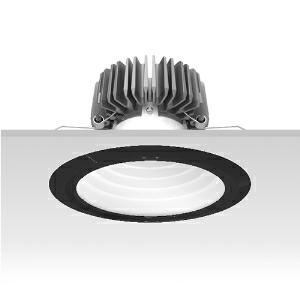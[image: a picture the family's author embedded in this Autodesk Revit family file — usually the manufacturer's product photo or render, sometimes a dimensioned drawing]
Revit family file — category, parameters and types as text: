
# Revit family: 3f_filippi_-_3f_reno_bianco_ampio_3f_filippi_-_30641_a01026_-_3f_reno_200_wh_4000-930_wide___vt_bk_7989
name_source: partatom
category: Lighting Fixtures
units: mm (PartAtom-declared; Revit-internal decimal feet)

## family parameters
Cut with Voids When Loaded = No
Host = Face
Light Source = No
Part Type = Normal
Room Calculation Point = No
Round Connector Dimension = Use Diameter
Shared = No

## types (1)
- 3F Filippi - 3F Reno Bianco Ampio (1 x LED, 3064 lm, 43 W, 3000 K)
    Apparent Load = 43 VA
    Approval mark = CE
    CIE Flux Codes = 75 94 99 100 100
    Color Rendering = 90
    Color Temperature = 3000 K
    Control Gear = Electronic ballast
    Default Elevation = 1800 mm
    Description = ILLUMINOTECHNICAL
Luminous efficiency 100% (DLOR 100%, ULOR 0%).
Initial luminous flux of the luminaire 3064 lm.
Direct symmetric wide distribution.
Installation Interdistance Transv.D = 1.56 x hu - Long.D = 1.56 x hu.
Tabular UGR (CIE 117 - 4H-8H; S=0.25H; 70/50/20): RUG 22.4 - 22.3.
Beam angle: 74° - 74°.
Luminous efficacy 71 lm/W.
Lifetime (L90/B10): 30000 h. (tq+25°C)
Lifetime (L85/B10): 50000 h. (tq+25°C)
Lifetime (L70/B10): 80000 h. (tq+25°C)
Sudden decreased luminous flux after 50000 hours: 0% (C0).
Photobiological safety in compliance with IEC/TR 62778: RG1 low risk, (IEC 62471).
In compliance with IEC/EN 62722-2-1 - IEC/EN 62717 standards.

SOURCE
Compact LED module 4000/930.
Energy efficiency class (UE 2019/2020 - UE 2019/2015): F.
CIE 13.3 Colour rendering index: CRI >90 (R9 >50%).
IES TM-30 Fidelity Index: Rf = 92 Rg = 101.
CCT nominal colour temperature 3000 K.
Colour initial tolerance (MacAdam): SDCM 3.
Zhaga Book 3 compliant.

MECHANICAL
Passive heat dissipator in die-casting aluminium, oversized, for optimum thermal management of the LED module.
Parabolic element with graduated/concentric rings in white polycarbonate.
Transparent external lens with glossy and satin differentiated surfaces, with a cooling and anti-insect system in methacrylate (PMMA).
Fastening spring clips in stainless steel.
Dimensions: diameter 226 mm, height 146 mm. Weight 1.705 kg.
IP44 protection degree for exposed part, IP20 for recessed part.
Mechanical strength to impacts IK06 (1 joule).
Glow-wire test resistance 650°C.

ELECTRICAL
Wiring on a separate unit.
Halogen Free electronic wiring 230V-50/60Hz, power factor 0.95, THD <25%, constant output current, SELV, class II, 1 driver.
Power of the luminaire 43 W.
ENEC - CE.
SAFE FLICKER: PstLM=<1 and SVM=<0.4 (IEC TR 61547-1 and IEC TR 63158), to ensure a more comfortable and safe light.
Luminaire compliant with EN 60598-2-22 for power supply from a centralised emergency system CPSS (Central Power Supply System), not incorporated in the luminaire - high risk areas excluded. The default power and flux are 100% in AC and 100% in DC.
Ambient temperature from 0°C to +25°C.
Temperature class T6 max 85°C.
Relative humidity UR: <85%.

INSTALLATION
Pull-up recessed fitting.
False ceiling carving: 200 mm.
All accessories dedicated to this product are available on the Catalog and on our website www.3F-Filippi.com.

ACCESSORIES
A01026 - VT transparent glass, tempered, not flammable, locked and in line with the trim, in black polycarbonate.

APPLICATIONS
Environments: architectural, commercial, exhibition areas, transit areas, corridors, shops, display windows, service areas.
In false ceilings with narrow voids.

WARNING
Luminaire designed for disposal/recycling at end-of-life.
Replaceable (LED only) light source by a professional. Replaceable control gear by a professional.
    Height = 0 mm  [stored 0 ft]
    Lamp = 1 x LED
    Lamp Light Flux = 3064 lm
    Lamp Power = 43 W
    Lamp count = 1
    Length = 226 mm
    Lifetime = 50000 h
    Luminous efficacy = 71 lm/W
    Manufacturer = 3F Filippi
    ModVariant = No
    Model = 3F Filippi - 30641+A01026 - 3F Reno 200 WH 4000-930 WIDE + VT BK
    Mounting Place = Ceiling
    Mounting Type = Recessed
    Number of Poles = 1
    OnlyDefault = Yes
    Power Factor = 1
    Product Name = 3F Filippi - 3F Reno Bianco Ampio
    Product group = recessed luminaire
    ProductGroupID = 4
    Protection Class = Protection class II
    Protection Degree = IP 20
    RLX_Detail_Level = 1
    RLX_Emergency_Light_Flux = 0 lm
    RLX_Emergency_Type = 0
    RLX_Emergency_Type_DB = No
    RlxData = <blob elided: 100677 chars, md5=1bf3c242>
    Socket = socket
    Standby Power = 0 W
    System Light Flux = 3064 lm
    System Power = 43 W
    Type Comments = Product without accessories
    Type Image = 3ffilippi_3f_reno_200_wh__a01026.jpg
    URL = http://relux.com
    VarID = ---
    Voltage = 0 V
    Weight = 0.00 kg
    Width = 0 mm  [stored 0 ft]

note: [stored X ft] marks values corroborated as IEEE doubles in the binary element streams (Revit-internal decimal feet)

## geometry (parser evidence)
native form markers: Blend x4, Sweep x9
no freeform markers — native parametric forms only
